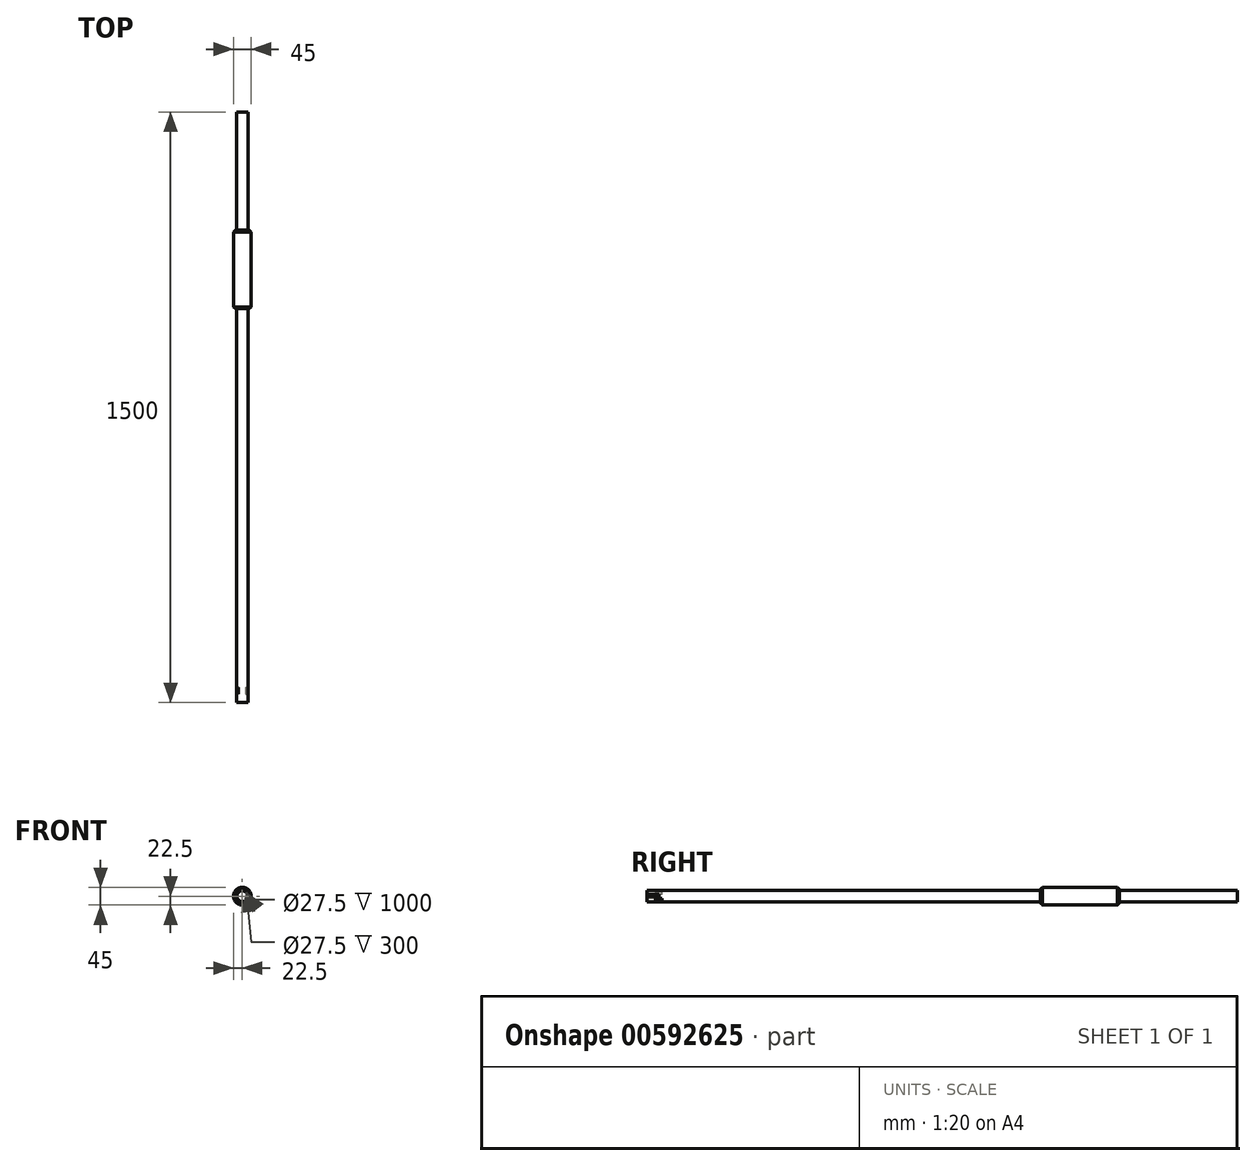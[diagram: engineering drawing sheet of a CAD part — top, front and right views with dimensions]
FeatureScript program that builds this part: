
annotation { "Feature Type Name" : "Feature", "Feature Type Description" : "" }
export const myFeature = defineFeature(function(context is Context, id is Id, definition is map)
    precondition{}
    {
        {
            var Q0;
            Q0=qCreatedBy(makeId("Front.planeOp"),FACE);
            var sketch = newSketch(context, id + "F0", { "sketchPlane" : qUnion([Q0])});
            skCircle(sketch, "E0", {"center": v(0, 0) * mm, "radius": 15 * mm});
            skSolve(sketch);
        }
        {
            var Q0;
            Q0=makeQuery(id+"F0.imprint","IMPRINT",FACE,{"disambiguationData":[TD([[makeQuery(id+"F0.imprint","IMPRINT",EDGE,{"derivedFrom":sQuery(id+"F0.wireOp",EDGE,"E0")}),1.0]])]});
            extrude(context, id + "F1", {"entities" : qUnion([Q0]), "oppositeDirection" : true, "depth" : 1500 * mm, "offsetDistance" : 25 * mm});
        }
        {
            var Q0;
            Q0=makeQuery(id+"F1.opExtrude","CAP_FACE",FACE,{"disambiguationData":[OSD([sQuery(id+"F0.wireOp",EDGE,"E0")])],"isStart":true});
            var sketch = newSketch(context, id + "F2", { "sketchPlane" : qUnion([Q0])});
            skCircle(sketch, "E1", {"center": v(0, 0) * mm, "radius": 13.75 * mm});
            skSolve(sketch);
        }
        {
            var Q0;
            Q0=makeQuery(id+"F2.imprint","IMPRINT",FACE,{"disambiguationData":[TD([[makeQuery(id+"F2.imprint","IMPRINT",EDGE,{"derivedFrom":sQuery(id+"F2.wireOp",EDGE,"E1")}),1.0]])]});
            extrude(context, id + "F3", {"entities" : qUnion([Q0]), "operationType" : NewBodyOperationType.REMOVE, "oppositeDirection" : true, "depth" : 3000 * mm, "offsetDistance" : 25 * mm});
        }
        {
            var Q0;
            Q0=qCreatedBy(makeId("Right.planeOp"),FACE);
            cPlane(context, id + "F4", {"entities" : qUnion([Q0]), "cplaneType" : CPlaneType.OFFSET, "offset" : 15 * mm, "width" : 150 * mm, "height" : 150 * mm});
        }
        {
            var Q0;
            Q0=qCreatedBy(makeId("Right.planeOp"),FACE);
            cPlane(context, id + "F5", {"entities" : qUnion([Q0]), "cplaneType" : CPlaneType.OFFSET, "offset" : 15 * mm, "oppositeDirection" : true, "width" : 150 * mm, "height" : 150 * mm});
        }
        {
            var Q0;
            Q0=qCreatedBy(id+"F4.planeOp",FACE);
            var sketch = newSketch(context, id + "F6", { "sketchPlane" : qUnion([Q0])});
            skLineSegment(sketch, "E2", {"start": v(0, 5) * mm, "end": v(30, 5) * mm});
            skLineSegment(sketch, "E3", {"start": v(30, 5) * mm, "end": v(30, -5) * mm});
            skLineSegment(sketch, "E4", {"start": v(30, -5) * mm, "end": v(38, -5) * mm});
            skLineSegment(sketch, "E5", {"start": v(38, -5) * mm, "end": v(38, -11) * mm});
            skLineSegment(sketch, "E6", {"start": v(38, -11) * mm, "end": v(22, -11) * mm});
            skLineSegment(sketch, "E7", {"start": v(22, -11) * mm, "end": v(22, -1) * mm});
            skLineSegment(sketch, "E8", {"start": v(22, -1) * mm, "end": v(0, -1) * mm});
            skLineSegment(sketch, "E9", {"start": v(0, -1) * mm, "end": v(0, 5) * mm});
            skSolve(sketch);
        }
        {
            var Q0;
            Q0 = qSketchRegion(id + "F6", true);
            extrude(context, id + "F7", {"entities" : qUnion([Q0]), "operationType" : NewBodyOperationType.REMOVE, "oppositeDirection" : true, "depth" : 10 * mm, "offsetDistance" : 25 * mm});
        }
        {
            var Q0;
            Q0=qCreatedBy(id+"F5.planeOp",FACE);
            var sketch = newSketch(context, id + "F8", { "sketchPlane" : qUnion([Q0])});
            skLineSegment(sketch, "E10", {"start": v(0, 1) * mm, "end": v(22, 1) * mm});
            skLineSegment(sketch, "E11", {"start": v(22, 1) * mm, "end": v(22, 11) * mm});
            skLineSegment(sketch, "E12", {"start": v(22, 11) * mm, "end": v(38, 11) * mm});
            skLineSegment(sketch, "E13", {"start": v(38, 11) * mm, "end": v(38, 5) * mm});
            skLineSegment(sketch, "E14", {"start": v(38, 5) * mm, "end": v(30, 5) * mm});
            skLineSegment(sketch, "E15", {"start": v(30, 5) * mm, "end": v(30, -5) * mm});
            skLineSegment(sketch, "E16", {"start": v(30, -5) * mm, "end": v(0, -5) * mm});
            skLineSegment(sketch, "E17", {"start": v(0, -5) * mm, "end": v(0, 1) * mm});
            skSolve(sketch);
        }
        {
            var Q0;
            Q0 = qSketchRegion(id + "F8", true);
            extrude(context, id + "F9", {"entities" : qUnion([Q0]), "operationType" : NewBodyOperationType.REMOVE, "depth" : 10 * mm, "offsetDistance" : 25 * mm});
        }
        {
            var Q0;
            Q0=qCreatedBy(makeId("Front.planeOp"),FACE);
            cPlane(context, id + "F10", {"entities" : qUnion([Q0]), "cplaneType" : CPlaneType.OFFSET, "offset" : 1500 * mm, "oppositeDirection" : true, "width" : 150 * mm, "height" : 150 * mm});
        }
        {
            var Q0;
            Q0=qCreatedBy(id+"F10.planeOp",FACE);
            cPlane(context, id + "F11", {"entities" : qUnion([Q0]), "cplaneType" : CPlaneType.OFFSET, "offset" : 300 * mm, "width" : 150 * mm, "height" : 150 * mm});
        }
        {
            var Q0;
            Q0=qCreatedBy(id+"F11.planeOp",FACE);
            var sketch = newSketch(context, id + "F12", { "sketchPlane" : qUnion([Q0])});
            skCircle(sketch, "E18", {"center": v(0, 0) * mm, "radius": 22.5 * mm});
            skSolve(sketch);
        }
        {
            var Q0;
            Q0 = qSketchRegion(id + "F12", true);
            extrude(context, id + "F13", {"entities" : qUnion([Q0]), "operationType" : NewBodyOperationType.ADD, "depth" : 200 * mm, "offsetDistance" : 25 * mm});
        }
        {
            var Q0;
            Q0=makeQuery(id+"F13.opExtrude","SWEPT_FACE",FACE,{"disambiguationData":[OSD([sQuery(id+"F12.wireOp",EDGE,"E18")])]});
            chamfer(context, id + "F14", {"entities" : qUnion([Q0]), "width" : 5 * mm, "tangentPropagation" : true});
        }
    });
